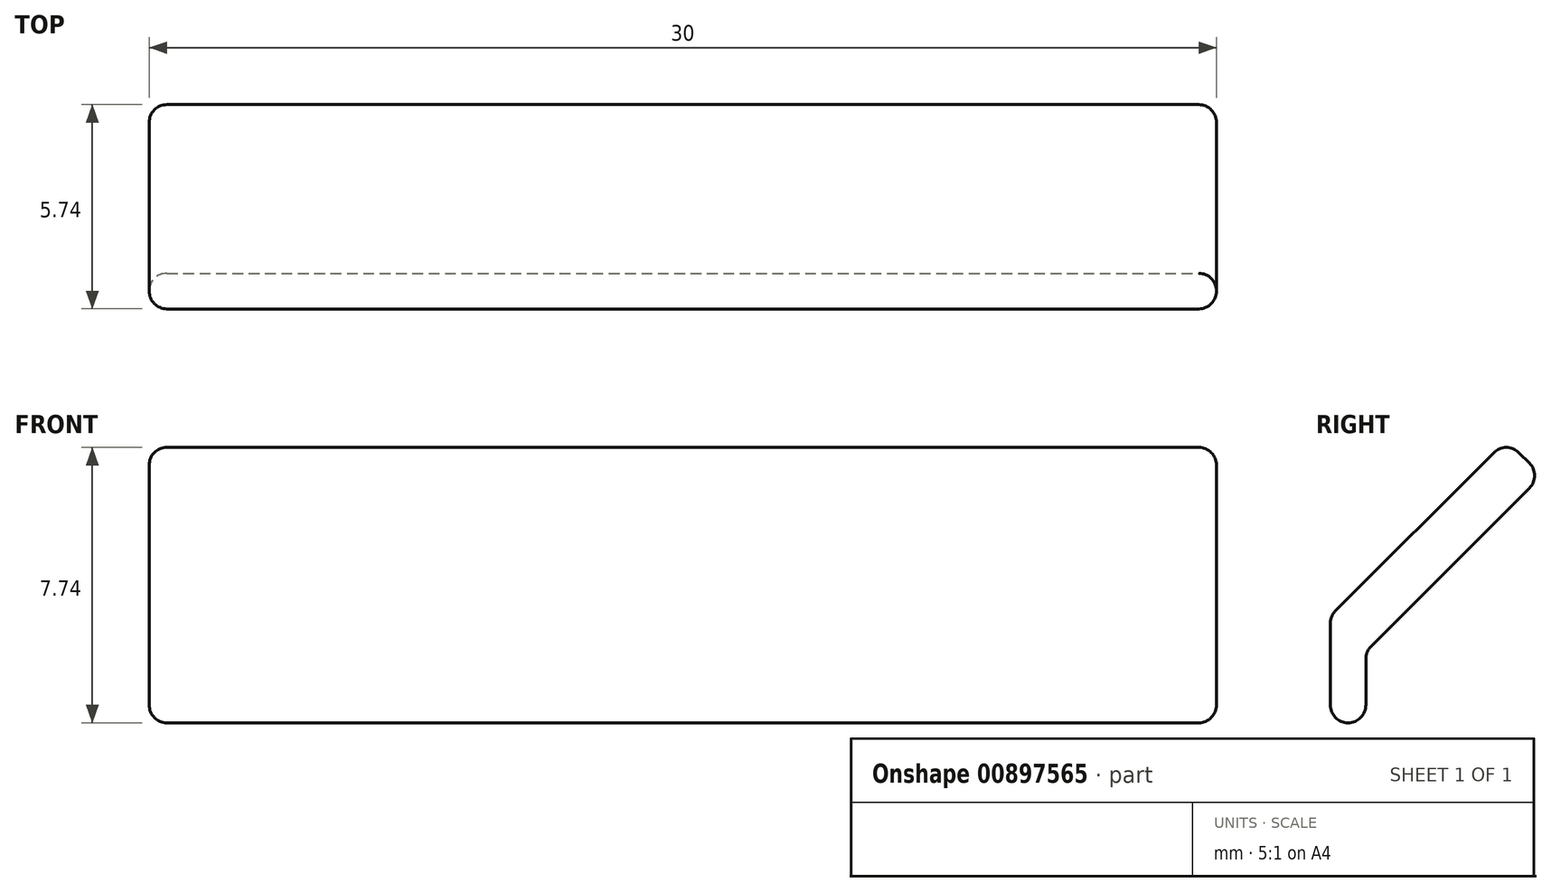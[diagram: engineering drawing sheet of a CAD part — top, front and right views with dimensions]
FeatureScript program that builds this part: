
annotation { "Feature Type Name" : "Feature", "Feature Type Description" : "" }
export const myFeature = defineFeature(function(context is Context, id is Id, definition is map)
    precondition{}
    {
        {
            var Q0;
            Q0=qCreatedBy(makeId("Top.planeOp"),FACE);
            var sketch = newSketch(context, id + "F0", { "sketchPlane" : qUnion([Q0])});
            skLineSegment(sketch, "E0.bottom", {"start": v(-48.55, 20.99) * mm, "end": v(-18.55, 20.99) * mm});
            skLineSegment(sketch, "E0.top", {"start": v(-48.55, 19.99) * mm, "end": v(-18.55, 19.99) * mm});
            skLineSegment(sketch, "E0.left", {"start": v(-48.55, 20.99) * mm, "end": v(-48.55, 19.99) * mm});
            skLineSegment(sketch, "E0.right", {"start": v(-18.55, 20.99) * mm, "end": v(-18.55, 19.99) * mm});
            skSolve(sketch);
        }
        {
            var Q0;
            Q0 = qSketchRegion(id + "F0", true);
            extrude(context, id + "F1", {"entities" : qUnion([Q0]), "depth" : 5 * mm, "offsetDistance" : 25 * mm});
        }
        {
            var Q0;
            Q0=makeQuery(id+"F1.opExtrude","CAP_EDGE",EDGE,{"disambiguationData":[OSD([sQuery(id+"F0.wireOp",EDGE,"E0.bottom")])],"isStart":false});
            chamfer(context, id + "F2", {"entities" : qUnion([Q0]), "width" : 3 * mm, "tangentPropagation" : true});
        }
        {
            var Q0;
            Q0=makeQuery(id+"F2.opChamfer","BLEND_FACE",FACE,{"disambiguationData":[OSD([sQuery(id+"F0.wireOp",EDGE,"E0.bottom")])]});
            var sketch = newSketch(context, id + "F3", { "sketchPlane" : qUnion([Q0])});
            skLineSegment(sketch, "E1.bottom", {"start": v(18.55, -13.43) * mm, "end": v(48.55, -13.43) * mm});
            skLineSegment(sketch, "E1.top", {"start": v(18.55, -12.01) * mm, "end": v(48.55, -12.01) * mm});
            skLineSegment(sketch, "E1.left", {"start": v(18.55, -13.43) * mm, "end": v(18.55, -12.01) * mm});
            skLineSegment(sketch, "E1.right", {"start": v(48.55, -13.43) * mm, "end": v(48.55, -12.01) * mm});
            skSolve(sketch);
        }
        {
            var Q0;
            Q0 = qSketchRegion(id + "F3", true);
            extrude(context, id + "F4", {"entities" : qUnion([Q0]), "operationType" : NewBodyOperationType.ADD, "depth" : 7 * mm, "offsetDistance" : 25 * mm});
        }
        {
            var Q0;
            Q0=makeQuery(id+"F4.opExtrude","SWEPT_FACE",FACE,{"disambiguationData":[OSD([sQuery(id+"F3.wireOp",EDGE,"E1.bottom")])]});
            var sketch = newSketch(context, id + "F5", { "sketchPlane" : qUnion([Q0])});
            skLineSegment(sketch, "E2.bottom", {"start": v(-24.04, -23.25) * mm, "end": v(-24.14, -23.25) * mm});
            skLineSegment(sketch, "E2.top", {"start": v(-24.04, -16.25) * mm, "end": v(-24.14, -16.25) * mm});
            skLineSegment(sketch, "E2.left", {"start": v(-24.04, -23.25) * mm, "end": v(-24.04, -16.25) * mm});
            skLineSegment(sketch, "E2.right", {"start": v(-24.14, -23.25) * mm, "end": v(-24.14, -16.25) * mm});
            skLineSegment(sketch, "E3.1.0.0", {"start": v(-29.14, -23.25) * mm, "end": v(-29.14, -16.25) * mm});
            skLineSegment(sketch, "E3.1.0.1", {"start": v(-29.04, -23.25) * mm, "end": v(-29.04, -16.25) * mm});
            skLineSegment(sketch, "E3.1.0.2", {"start": v(-29.04, -23.25) * mm, "end": v(-29.14, -23.25) * mm});
            skLineSegment(sketch, "E3.1.0.3", {"start": v(-29.04, -16.25) * mm, "end": v(-29.14, -16.25) * mm});
            skLineSegment(sketch, "E3.2.0.0", {"start": v(-34.14, -23.25) * mm, "end": v(-34.14, -16.25) * mm});
            skLineSegment(sketch, "E3.2.0.1", {"start": v(-34.04, -23.25) * mm, "end": v(-34.04, -16.25) * mm});
            skLineSegment(sketch, "E3.2.0.2", {"start": v(-34.04, -23.25) * mm, "end": v(-34.14, -23.25) * mm});
            skLineSegment(sketch, "E3.2.0.3", {"start": v(-34.04, -16.25) * mm, "end": v(-34.14, -16.25) * mm});
            skLineSegment(sketch, "E3.3.0.0", {"start": v(-39.14, -23.25) * mm, "end": v(-39.14, -16.25) * mm});
            skLineSegment(sketch, "E3.3.0.1", {"start": v(-39.04, -23.25) * mm, "end": v(-39.04, -16.25) * mm});
            skLineSegment(sketch, "E3.3.0.2", {"start": v(-39.04, -23.25) * mm, "end": v(-39.14, -23.25) * mm});
            skLineSegment(sketch, "E3.3.0.3", {"start": v(-39.04, -16.25) * mm, "end": v(-39.14, -16.25) * mm});
            skLineSegment(sketch, "E3.4.0.0", {"start": v(-44.14, -23.25) * mm, "end": v(-44.14, -16.25) * mm});
            skLineSegment(sketch, "E3.4.0.1", {"start": v(-44.04, -23.25) * mm, "end": v(-44.04, -16.25) * mm});
            skLineSegment(sketch, "E3.4.0.2", {"start": v(-44.04, -23.25) * mm, "end": v(-44.14, -23.25) * mm});
            skLineSegment(sketch, "E3.4.0.3", {"start": v(-44.04, -16.25) * mm, "end": v(-44.14, -16.25) * mm});
            skLineSegment(sketch, "E3.direction1", {"start": v(-24.14, -23.25) * mm, "end": v(-29.14, -23.25) * mm, "construction": true});
            skSolve(sketch);
        }
        {
            var Q0;
            Q0 = qSketchRegion(id + "F5", true);
            extrude(context, id + "F6", {"entities" : qUnion([Q0]), "operationType" : NewBodyOperationType.REMOVE, "endBound" : BoundingType.THROUGH_ALL, "oppositeDirection" : true, "depth" : 25 * mm, "offsetDistance" : 25 * mm});
        }
        {
            var Q0;
            Q0=makeQuery(id+"F1.opExtrude","CAP_EDGE",EDGE,{"disambiguationData":[OSD([sQuery(id+"F0.wireOp",EDGE,"E0.top")])],"isStart":true});
            var Q1;
            Q1=makeQuery(id+"F1.opExtrude","SWEPT_EDGE",EDGE,{"disambiguationData":[OSD([sQuery(id+"F0.wireOp",EDGE,"E0.top"),sQuery(id+"F0.wireOp",EDGE,"E0.left")])]});
            var Q2;
            Q2=makeQuery(id+"F1.opExtrude","SWEPT_EDGE",EDGE,{"disambiguationData":[OSD([sQuery(id+"F0.wireOp",EDGE,"E0.top"),sQuery(id+"F0.wireOp",EDGE,"E0.right")])]});
            var Q3;
            Q3=makeQuery(id+"F1.opExtrude","SWEPT_EDGE",EDGE,{"disambiguationData":[OSD([sQuery(id+"F0.wireOp",EDGE,"E0.bottom"),sQuery(id+"F0.wireOp",EDGE,"E0.right")])]});
            var Q4;
            Q4=makeQuery(id+"F1.opExtrude","CAP_EDGE",EDGE,{"disambiguationData":[OSD([sQuery(id+"F0.wireOp",EDGE,"E0.right")])],"isStart":true});
            var Q5;
            Q5=makeQuery(id+"F4.opExtrude","SWEPT_EDGE",EDGE,{"disambiguationData":[OSD([sQuery(id+"F3.wireOp",EDGE,"E1.top"),sQuery(id+"F3.wireOp",EDGE,"E1.left")])]});
            var Q6;
            Q6=makeQuery(id+"F4.opExtrude","SWEPT_EDGE",EDGE,{"disambiguationData":[OSD([sQuery(id+"F3.wireOp",EDGE,"E1.bottom"),sQuery(id+"F3.wireOp",EDGE,"E1.left")])]});
            var Q7;
            Q7=makeQuery(id+"F1.opExtrude","SWEPT_EDGE",EDGE,{"disambiguationData":[OSD([sQuery(id+"F0.wireOp",EDGE,"E0.bottom"),sQuery(id+"F0.wireOp",EDGE,"E0.left")])]});
            var Q8;
            Q8=makeQuery(id+"F4.opExtrude","SWEPT_EDGE",EDGE,{"disambiguationData":[OSD([sQuery(id+"F3.wireOp",EDGE,"E1.bottom"),sQuery(id+"F3.wireOp",EDGE,"E1.right")])]});
            var Q9;
            Q9=makeQuery(id+"F4.opExtrude","SWEPT_EDGE",EDGE,{"disambiguationData":[OSD([sQuery(id+"F3.wireOp",EDGE,"E1.top"),sQuery(id+"F3.wireOp",EDGE,"E1.right")])]});
            var Q10;
            Q10=makeQuery(id+"F1.opExtrude","CAP_EDGE",EDGE,{"disambiguationData":[OSD([sQuery(id+"F0.wireOp",EDGE,"E0.bottom")])],"isStart":true});
            var Q11;
            Q11=makeQuery(id+"F1.opExtrude","CAP_EDGE",EDGE,{"disambiguationData":[OSD([sQuery(id+"F0.wireOp",EDGE,"E0.left")])],"isStart":true});
            var Q12;
            {var subQ0=sQuery(id+"F3.wireOp",EDGE,"E1.bottom");var subQ1=sQuery(id+"F0.wireOp",EDGE,"E0.bottom");var subQ2=makeQuery(id+"F1.opExtrude","SWEPT_FACE",FACE,{"disambiguationData":[OSD([subQ1])]});Q12=makeQuery(id+"F6.boolean.opBoolean","SPLIT",EDGE,{"disambiguationData":[TD([makeQuery(id+"F6.opExtrude","SWEPT_FACE",FACE,{"disambiguationData":[OSD([sQuery(id+"F5.wireOp",EDGE,"E3.2.0.0")])]})])],"derivedFrom":makeQuery(id+"F4.boolean.opBoolean","MERGE",EDGE,{"derivedFrom":[makeQuery(id+"F2.opChamfer","BLEND_EDGE",EDGE,{"blendedFrom":[makeQuery(id+"F1.opExtrude","CAP_EDGE",EDGE,{"disambiguationData":[OSD([subQ1])],"isStart":false}),subQ2],"blendedInto":[subQ2]}),makeQuery(id+"F4.opExtrude","CAP_EDGE",EDGE,{"disambiguationData":[OSD([subQ0])],"isStart":true})]})});}
            var Q13;
            {var subQ0=sQuery(id+"F0.wireOp",EDGE,"E0.bottom");var subQ1=makeQuery(id+"F1.opExtrude","SWEPT_FACE",FACE,{"disambiguationData":[OSD([subQ0])]});var subQ2=sQuery(id+"F3.wireOp",EDGE,"E1.bottom");Q13=makeQuery(id+"F6.boolean.opBoolean","SPLIT",EDGE,{"disambiguationData":[TD([makeQuery(id+"F6.opExtrude","SWEPT_FACE",FACE,{"disambiguationData":[OSD([sQuery(id+"F5.wireOp",EDGE,"E3.3.0.0")])]})])],"derivedFrom":makeQuery(id+"F4.boolean.opBoolean","MERGE",EDGE,{"derivedFrom":[makeQuery(id+"F2.opChamfer","BLEND_EDGE",EDGE,{"blendedFrom":[makeQuery(id+"F1.opExtrude","CAP_EDGE",EDGE,{"disambiguationData":[OSD([subQ0])],"isStart":false}),subQ1],"blendedInto":[subQ1]}),makeQuery(id+"F4.opExtrude","CAP_EDGE",EDGE,{"disambiguationData":[OSD([subQ2])],"isStart":true})]})});}
            var Q14;
            {var subQ0=sQuery(id+"F3.wireOp",EDGE,"E1.bottom");var subQ1=sQuery(id+"F0.wireOp",EDGE,"E0.bottom");var subQ2=makeQuery(id+"F1.opExtrude","SWEPT_FACE",FACE,{"disambiguationData":[OSD([subQ1])]});Q14=makeQuery(id+"F6.boolean.opBoolean","SPLIT",EDGE,{"disambiguationData":[TD([makeQuery(id+"F1.opExtrude","SWEPT_FACE",FACE,{"disambiguationData":[OSD([sQuery(id+"F0.wireOp",EDGE,"E0.left")])]})])],"derivedFrom":makeQuery(id+"F4.boolean.opBoolean","MERGE",EDGE,{"derivedFrom":[makeQuery(id+"F2.opChamfer","BLEND_EDGE",EDGE,{"blendedFrom":[makeQuery(id+"F1.opExtrude","CAP_EDGE",EDGE,{"disambiguationData":[OSD([subQ1])],"isStart":false}),subQ2],"blendedInto":[subQ2]}),makeQuery(id+"F4.opExtrude","CAP_EDGE",EDGE,{"disambiguationData":[OSD([subQ0])],"isStart":true})]})});}
            var Q15;
            {var subQ0=sQuery(id+"F3.wireOp",EDGE,"E1.bottom");var subQ1=sQuery(id+"F0.wireOp",EDGE,"E0.bottom");var subQ2=makeQuery(id+"F1.opExtrude","SWEPT_FACE",FACE,{"disambiguationData":[OSD([subQ1])]});Q15=makeQuery(id+"F6.boolean.opBoolean","SPLIT",EDGE,{"disambiguationData":[TD([makeQuery(id+"F6.opExtrude","SWEPT_FACE",FACE,{"disambiguationData":[OSD([sQuery(id+"F5.wireOp",EDGE,"E3.1.0.0")])]})])],"derivedFrom":makeQuery(id+"F4.boolean.opBoolean","MERGE",EDGE,{"derivedFrom":[makeQuery(id+"F2.opChamfer","BLEND_EDGE",EDGE,{"blendedFrom":[makeQuery(id+"F1.opExtrude","CAP_EDGE",EDGE,{"disambiguationData":[OSD([subQ1])],"isStart":false}),subQ2],"blendedInto":[subQ2]}),makeQuery(id+"F4.opExtrude","CAP_EDGE",EDGE,{"disambiguationData":[OSD([subQ0])],"isStart":true})]})});}
            var Q16;
            {var subQ0=sQuery(id+"F3.wireOp",EDGE,"E1.bottom");var subQ1=sQuery(id+"F0.wireOp",EDGE,"E0.bottom");var subQ2=makeQuery(id+"F1.opExtrude","SWEPT_FACE",FACE,{"disambiguationData":[OSD([subQ1])]});Q16=makeQuery(id+"F6.boolean.opBoolean","SPLIT",EDGE,{"disambiguationData":[TD([makeQuery(id+"F6.opExtrude","SWEPT_FACE",FACE,{"disambiguationData":[OSD([sQuery(id+"F5.wireOp",EDGE,"E2.right")])]})])],"derivedFrom":makeQuery(id+"F4.boolean.opBoolean","MERGE",EDGE,{"derivedFrom":[makeQuery(id+"F2.opChamfer","BLEND_EDGE",EDGE,{"blendedFrom":[makeQuery(id+"F1.opExtrude","CAP_EDGE",EDGE,{"disambiguationData":[OSD([subQ1])],"isStart":false}),subQ2],"blendedInto":[subQ2]}),makeQuery(id+"F4.opExtrude","CAP_EDGE",EDGE,{"disambiguationData":[OSD([subQ0])],"isStart":true})]})});}
            var Q17;
            {var subQ0=sQuery(id+"F3.wireOp",EDGE,"E1.bottom");var subQ1=sQuery(id+"F0.wireOp",EDGE,"E0.bottom");var subQ2=makeQuery(id+"F1.opExtrude","SWEPT_FACE",FACE,{"disambiguationData":[OSD([subQ1])]});Q17=makeQuery(id+"F6.boolean.opBoolean","SPLIT",EDGE,{"disambiguationData":[TD([makeQuery(id+"F1.opExtrude","SWEPT_FACE",FACE,{"disambiguationData":[OSD([sQuery(id+"F0.wireOp",EDGE,"E0.right")])]})])],"derivedFrom":makeQuery(id+"F4.boolean.opBoolean","MERGE",EDGE,{"derivedFrom":[makeQuery(id+"F2.opChamfer","BLEND_EDGE",EDGE,{"blendedFrom":[makeQuery(id+"F1.opExtrude","CAP_EDGE",EDGE,{"disambiguationData":[OSD([subQ1])],"isStart":false}),subQ2],"blendedInto":[subQ2]}),makeQuery(id+"F4.opExtrude","CAP_EDGE",EDGE,{"disambiguationData":[OSD([subQ0])],"isStart":true})]})});}
            var Q18;
            {var subQ0=sQuery(id+"F3.wireOp",EDGE,"E1.top");Q18=makeQuery(id+"F6.boolean.opBoolean","SPLIT",EDGE,{"disambiguationData":[TD([makeQuery(id+"F6.opExtrude","SWEPT_FACE",FACE,{"disambiguationData":[OSD([sQuery(id+"F5.wireOp",EDGE,"E3.1.0.0")])]})])],"derivedFrom":makeQuery(id+"F4.opExtrude","CAP_EDGE",EDGE,{"disambiguationData":[OSD([subQ0])],"isStart":false})});}
            var Q19;
            {var subQ0=sQuery(id+"F3.wireOp",EDGE,"E1.top");Q19=makeQuery(id+"F6.boolean.opBoolean","SPLIT",EDGE,{"disambiguationData":[TD([makeQuery(id+"F6.opExtrude","SWEPT_FACE",FACE,{"disambiguationData":[OSD([sQuery(id+"F5.wireOp",EDGE,"E2.right")])]})])],"derivedFrom":makeQuery(id+"F4.opExtrude","CAP_EDGE",EDGE,{"disambiguationData":[OSD([subQ0])],"isStart":false})});}
            var Q20;
            {var subQ1=sQuery(id+"F3.wireOp",EDGE,"E1.top");Q20=makeQuery(id+"F6.boolean.opBoolean","SPLIT",EDGE,{"disambiguationData":[TD([makeQuery(id+"F1.opExtrude","SWEPT_FACE",FACE,{"disambiguationData":[OSD([sQuery(id+"F0.wireOp",EDGE,"E0.right")])]})])],"derivedFrom":makeQuery(id+"F4.opExtrude","CAP_EDGE",EDGE,{"disambiguationData":[OSD([subQ1])],"isStart":false})});}
            var Q21;
            {var subQ0=sQuery(id+"F3.wireOp",EDGE,"E1.top");Q21=makeQuery(id+"F6.boolean.opBoolean","SPLIT",EDGE,{"disambiguationData":[TD([makeQuery(id+"F6.opExtrude","SWEPT_FACE",FACE,{"disambiguationData":[OSD([sQuery(id+"F5.wireOp",EDGE,"E3.2.0.0")])]})])],"derivedFrom":makeQuery(id+"F4.opExtrude","CAP_EDGE",EDGE,{"disambiguationData":[OSD([subQ0])],"isStart":false})});}
            var Q22;
            {var subQ0=sQuery(id+"F3.wireOp",EDGE,"E1.top");Q22=makeQuery(id+"F6.boolean.opBoolean","SPLIT",EDGE,{"disambiguationData":[TD([makeQuery(id+"F6.opExtrude","SWEPT_FACE",FACE,{"disambiguationData":[OSD([sQuery(id+"F5.wireOp",EDGE,"E3.3.0.0")])]})])],"derivedFrom":makeQuery(id+"F4.opExtrude","CAP_EDGE",EDGE,{"disambiguationData":[OSD([subQ0])],"isStart":false})});}
            var Q23;
            {var subQ0=sQuery(id+"F3.wireOp",EDGE,"E1.top");Q23=makeQuery(id+"F6.boolean.opBoolean","SPLIT",EDGE,{"disambiguationData":[TD([makeQuery(id+"F1.opExtrude","SWEPT_FACE",FACE,{"disambiguationData":[OSD([sQuery(id+"F0.wireOp",EDGE,"E0.left")])]})])],"derivedFrom":makeQuery(id+"F4.opExtrude","CAP_EDGE",EDGE,{"disambiguationData":[OSD([subQ0])],"isStart":false})});}
            var Q24;
            {var subQ0=sQuery(id+"F3.wireOp",EDGE,"E1.bottom");Q24=makeQuery(id+"F6.boolean.opBoolean","SPLIT",EDGE,{"disambiguationData":[TD([makeQuery(id+"F6.opExtrude","SWEPT_FACE",FACE,{"disambiguationData":[OSD([sQuery(id+"F5.wireOp",EDGE,"E3.3.0.0")])]})])],"derivedFrom":makeQuery(id+"F4.opExtrude","CAP_EDGE",EDGE,{"disambiguationData":[OSD([subQ0])],"isStart":false})});}
            var Q25;
            {var subQ1=sQuery(id+"F3.wireOp",EDGE,"E1.bottom");Q25=makeQuery(id+"F6.boolean.opBoolean","SPLIT",EDGE,{"disambiguationData":[TD([makeQuery(id+"F1.opExtrude","SWEPT_FACE",FACE,{"disambiguationData":[OSD([sQuery(id+"F0.wireOp",EDGE,"E0.left")])]})])],"derivedFrom":makeQuery(id+"F4.opExtrude","CAP_EDGE",EDGE,{"disambiguationData":[OSD([subQ1])],"isStart":false})});}
            var Q26;
            {var subQ0=sQuery(id+"F3.wireOp",EDGE,"E1.bottom");Q26=makeQuery(id+"F6.boolean.opBoolean","SPLIT",EDGE,{"disambiguationData":[TD([makeQuery(id+"F6.opExtrude","SWEPT_FACE",FACE,{"disambiguationData":[OSD([sQuery(id+"F5.wireOp",EDGE,"E3.2.0.0")])]})])],"derivedFrom":makeQuery(id+"F4.opExtrude","CAP_EDGE",EDGE,{"disambiguationData":[OSD([subQ0])],"isStart":false})});}
            var Q27;
            {var subQ0=sQuery(id+"F3.wireOp",EDGE,"E1.bottom");Q27=makeQuery(id+"F6.boolean.opBoolean","SPLIT",EDGE,{"disambiguationData":[TD([makeQuery(id+"F6.opExtrude","SWEPT_FACE",FACE,{"disambiguationData":[OSD([sQuery(id+"F5.wireOp",EDGE,"E3.1.0.0")])]})])],"derivedFrom":makeQuery(id+"F4.opExtrude","CAP_EDGE",EDGE,{"disambiguationData":[OSD([subQ0])],"isStart":false})});}
            var Q28;
            {var subQ0=sQuery(id+"F3.wireOp",EDGE,"E1.bottom");Q28=makeQuery(id+"F6.boolean.opBoolean","SPLIT",EDGE,{"disambiguationData":[TD([makeQuery(id+"F6.opExtrude","SWEPT_FACE",FACE,{"disambiguationData":[OSD([sQuery(id+"F5.wireOp",EDGE,"E2.right")])]})])],"derivedFrom":makeQuery(id+"F4.opExtrude","CAP_EDGE",EDGE,{"disambiguationData":[OSD([subQ0])],"isStart":false})});}
            var Q29;
            {var subQ1=sQuery(id+"F3.wireOp",EDGE,"E1.bottom");Q29=makeQuery(id+"F6.boolean.opBoolean","SPLIT",EDGE,{"disambiguationData":[TD([makeQuery(id+"F1.opExtrude","SWEPT_FACE",FACE,{"disambiguationData":[OSD([sQuery(id+"F0.wireOp",EDGE,"E0.right")])]})])],"derivedFrom":makeQuery(id+"F4.opExtrude","CAP_EDGE",EDGE,{"disambiguationData":[OSD([subQ1])],"isStart":false})});}
            var Q30;
            Q30=makeQuery(id+"F4.opExtrude","CAP_EDGE",EDGE,{"disambiguationData":[OSD([sQuery(id+"F3.wireOp",EDGE,"E1.left")])],"isStart":false});
            var Q31;
            Q31=makeQuery(id+"F4.opExtrude","CAP_EDGE",EDGE,{"disambiguationData":[OSD([sQuery(id+"F3.wireOp",EDGE,"E1.right")])],"isStart":false});
            var Q32;
            {var subQ0=sQuery(id+"F3.wireOp",EDGE,"E1.top");var subQ1=makeQuery(id+"F4.opExtrude","SWEPT_FACE",FACE,{"disambiguationData":[OSD([subQ0])]});var subQ2=makeQuery(id+"F1.opExtrude","SWEPT_FACE",FACE,{"disambiguationData":[OSD([sQuery(id+"F0.wireOp",EDGE,"E0.top")])]});Q32=makeQuery(id+"F6.boolean.opBoolean","SPLIT",EDGE,{"disambiguationData":[topologyDisambiguationEdgeConnected([subQ2,subQ1]),TD([makeQuery(id+"F1.opExtrude","SWEPT_FACE",FACE,{"disambiguationData":[OSD([sQuery(id+"F0.wireOp",EDGE,"E0.right")])]})])],"derivedFrom":makeQuery(id+"F4.boolean.opBoolean","MERGE",EDGE,{"derivedFrom":[makeQuery(id+"F2.opChamfer","BLEND_EDGE",EDGE,{"blendedFrom":[makeQuery(id+"F1.opExtrude","CAP_EDGE",EDGE,{"disambiguationData":[OSD([sQuery(id+"F0.wireOp",EDGE,"E0.bottom")])],"isStart":false}),subQ2],"blendedInto":[subQ2]}),makeQuery(id+"F4.opExtrude","CAP_EDGE",EDGE,{"disambiguationData":[OSD([subQ0])],"isStart":true})]})});}
            var Q33;
            {var subQ0=sQuery(id+"F3.wireOp",EDGE,"E1.top");var subQ1=makeQuery(id+"F4.opExtrude","SWEPT_FACE",FACE,{"disambiguationData":[OSD([subQ0])]});var subQ2=makeQuery(id+"F1.opExtrude","SWEPT_FACE",FACE,{"disambiguationData":[OSD([sQuery(id+"F0.wireOp",EDGE,"E0.top")])]});Q33=makeQuery(id+"F6.boolean.opBoolean","SPLIT",EDGE,{"disambiguationData":[topologyDisambiguationEdgeConnected([subQ2,subQ1]),TD([makeQuery(id+"F6.opExtrude","SWEPT_FACE",FACE,{"disambiguationData":[OSD([sQuery(id+"F5.wireOp",EDGE,"E2.right")])]})])],"derivedFrom":makeQuery(id+"F4.boolean.opBoolean","MERGE",EDGE,{"derivedFrom":[makeQuery(id+"F2.opChamfer","BLEND_EDGE",EDGE,{"blendedFrom":[makeQuery(id+"F1.opExtrude","CAP_EDGE",EDGE,{"disambiguationData":[OSD([sQuery(id+"F0.wireOp",EDGE,"E0.bottom")])],"isStart":false}),subQ2],"blendedInto":[subQ2]}),makeQuery(id+"F4.opExtrude","CAP_EDGE",EDGE,{"disambiguationData":[OSD([subQ0])],"isStart":true})]})});}
            var Q34;
            {var subQ0=sQuery(id+"F3.wireOp",EDGE,"E1.top");var subQ1=makeQuery(id+"F4.opExtrude","SWEPT_FACE",FACE,{"disambiguationData":[OSD([subQ0])]});var subQ2=makeQuery(id+"F1.opExtrude","SWEPT_FACE",FACE,{"disambiguationData":[OSD([sQuery(id+"F0.wireOp",EDGE,"E0.top")])]});Q34=makeQuery(id+"F6.boolean.opBoolean","SPLIT",EDGE,{"disambiguationData":[topologyDisambiguationEdgeConnected([subQ2,subQ1]),TD([makeQuery(id+"F6.opExtrude","SWEPT_FACE",FACE,{"disambiguationData":[OSD([sQuery(id+"F5.wireOp",EDGE,"E3.1.0.0")])]})])],"derivedFrom":makeQuery(id+"F4.boolean.opBoolean","MERGE",EDGE,{"derivedFrom":[makeQuery(id+"F2.opChamfer","BLEND_EDGE",EDGE,{"blendedFrom":[makeQuery(id+"F1.opExtrude","CAP_EDGE",EDGE,{"disambiguationData":[OSD([sQuery(id+"F0.wireOp",EDGE,"E0.bottom")])],"isStart":false}),subQ2],"blendedInto":[subQ2]}),makeQuery(id+"F4.opExtrude","CAP_EDGE",EDGE,{"disambiguationData":[OSD([subQ0])],"isStart":true})]})});}
            var Q35;
            {var subQ0=sQuery(id+"F3.wireOp",EDGE,"E1.top");var subQ1=makeQuery(id+"F4.opExtrude","SWEPT_FACE",FACE,{"disambiguationData":[OSD([subQ0])]});var subQ2=makeQuery(id+"F1.opExtrude","SWEPT_FACE",FACE,{"disambiguationData":[OSD([sQuery(id+"F0.wireOp",EDGE,"E0.top")])]});Q35=makeQuery(id+"F6.boolean.opBoolean","SPLIT",EDGE,{"disambiguationData":[topologyDisambiguationEdgeConnected([subQ2,subQ1]),TD([makeQuery(id+"F6.opExtrude","SWEPT_FACE",FACE,{"disambiguationData":[OSD([sQuery(id+"F5.wireOp",EDGE,"E3.2.0.0")])]})])],"derivedFrom":makeQuery(id+"F4.boolean.opBoolean","MERGE",EDGE,{"derivedFrom":[makeQuery(id+"F2.opChamfer","BLEND_EDGE",EDGE,{"blendedFrom":[makeQuery(id+"F1.opExtrude","CAP_EDGE",EDGE,{"disambiguationData":[OSD([sQuery(id+"F0.wireOp",EDGE,"E0.bottom")])],"isStart":false}),subQ2],"blendedInto":[subQ2]}),makeQuery(id+"F4.opExtrude","CAP_EDGE",EDGE,{"disambiguationData":[OSD([subQ0])],"isStart":true})]})});}
            var Q36;
            {var subQ0=sQuery(id+"F3.wireOp",EDGE,"E1.top");var subQ1=makeQuery(id+"F4.opExtrude","SWEPT_FACE",FACE,{"disambiguationData":[OSD([subQ0])]});var subQ2=makeQuery(id+"F1.opExtrude","SWEPT_FACE",FACE,{"disambiguationData":[OSD([sQuery(id+"F0.wireOp",EDGE,"E0.top")])]});Q36=makeQuery(id+"F6.boolean.opBoolean","SPLIT",EDGE,{"disambiguationData":[topologyDisambiguationEdgeConnected([subQ2,subQ1]),TD([makeQuery(id+"F6.opExtrude","SWEPT_FACE",FACE,{"disambiguationData":[OSD([sQuery(id+"F5.wireOp",EDGE,"E3.3.0.0")])]})])],"derivedFrom":makeQuery(id+"F4.boolean.opBoolean","MERGE",EDGE,{"derivedFrom":[makeQuery(id+"F2.opChamfer","BLEND_EDGE",EDGE,{"blendedFrom":[makeQuery(id+"F1.opExtrude","CAP_EDGE",EDGE,{"disambiguationData":[OSD([sQuery(id+"F0.wireOp",EDGE,"E0.bottom")])],"isStart":false}),subQ2],"blendedInto":[subQ2]}),makeQuery(id+"F4.opExtrude","CAP_EDGE",EDGE,{"disambiguationData":[OSD([subQ0])],"isStart":true})]})});}
            var Q37;
            {var subQ0=sQuery(id+"F3.wireOp",EDGE,"E1.top");var subQ1=makeQuery(id+"F4.opExtrude","SWEPT_FACE",FACE,{"disambiguationData":[OSD([subQ0])]});var subQ2=makeQuery(id+"F1.opExtrude","SWEPT_FACE",FACE,{"disambiguationData":[OSD([sQuery(id+"F0.wireOp",EDGE,"E0.top")])]});Q37=makeQuery(id+"F6.boolean.opBoolean","SPLIT",EDGE,{"disambiguationData":[topologyDisambiguationEdgeConnected([subQ2,subQ1]),TD([makeQuery(id+"F1.opExtrude","SWEPT_FACE",FACE,{"disambiguationData":[OSD([sQuery(id+"F0.wireOp",EDGE,"E0.left")])]})])],"derivedFrom":makeQuery(id+"F4.boolean.opBoolean","MERGE",EDGE,{"derivedFrom":[makeQuery(id+"F2.opChamfer","BLEND_EDGE",EDGE,{"blendedFrom":[makeQuery(id+"F1.opExtrude","CAP_EDGE",EDGE,{"disambiguationData":[OSD([sQuery(id+"F0.wireOp",EDGE,"E0.bottom")])],"isStart":false}),subQ2],"blendedInto":[subQ2]}),makeQuery(id+"F4.opExtrude","CAP_EDGE",EDGE,{"disambiguationData":[OSD([subQ0])],"isStart":true})]})});}
            fillet(context, id + "F7", {"entities" : qUnion([Q0, Q1, Q2, Q3, Q4, Q5, Q6, Q7, Q8, Q9, Q10, Q11, Q12, Q13, Q14, Q15, Q16, Q17, Q18, Q19, Q20, Q21, Q22, Q23, Q24, Q25, Q26, Q27, Q28, Q29, Q30, Q31, Q32, Q33, Q34, Q35, Q36, Q37]), "radius" : 0.5 * mm, "tangentPropagation" : true, "allowEdgeOverflow" : false});
        }
    });
